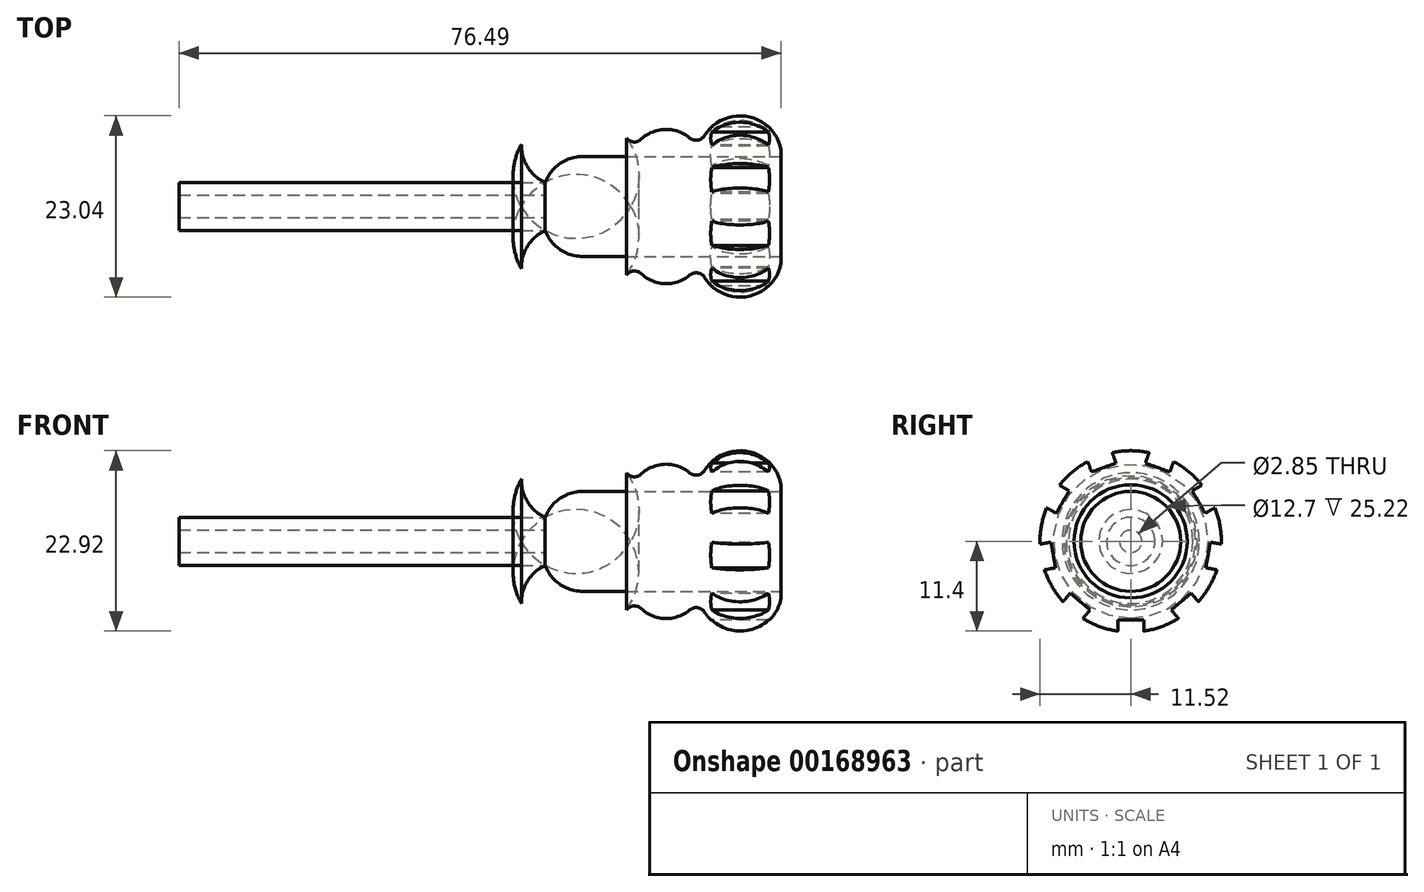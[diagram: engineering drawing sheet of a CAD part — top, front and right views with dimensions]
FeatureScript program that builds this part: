
annotation { "Feature Type Name" : "Feature", "Feature Type Description" : "" }
export const myFeature = defineFeature(function(context is Context, id is Id, definition is map)
    precondition{}
    {
        {
            var Q0;
            Q0=qCreatedBy(makeId("Front.planeOp"),FACE);
            var sketch = newSketch(context, id + "F0", { "sketchPlane" : qUnion([Q0])});
            skLineSegment(sketch, "E0.bottom", {"start": v(0, 0) * mm, "end": v(-76.5, 0) * mm});
            skLineSegment(sketch, "E0.top", {"start": v(0, 3.07) * mm, "end": v(-76.5, 3.07) * mm});
            skLineSegment(sketch, "E0.left", {"start": v(0, 0) * mm, "end": v(0, 3.07) * mm});
            skLineSegment(sketch, "E0.right", {"start": v(-76.5, 0) * mm, "end": v(-76.5, 3.07) * mm});
            skLineSegment(sketch, "E1.bottom", {"start": v(0, 0) * mm, "end": v(-33, 0) * mm});
            skLineSegment(sketch, "E1.top", {"start": v(0, 13.87) * mm, "end": v(-33, 13.87) * mm});
            skLineSegment(sketch, "E1.left", {"start": v(0, 0) * mm, "end": v(0, 13.87) * mm});
            skLineSegment(sketch, "E1.right", {"start": v(-33, 0) * mm, "end": v(-33, 13.87) * mm});
            skArc(sketch, "E2", {"start": v(-19.67, 8.7) * mm, "mid": v(-21.57, 10.52) * mm, "end": v(-23.95, 11.62) * mm});
            skArc(sketch, "E3", {"start": v(-11.61, 8.71) * mm, "mid": v(-14.73, 9.8) * mm, "end": v(-17.78, 8.54) * mm});
            skArc(sketch, "E4", {"start": v(0, 7.2) * mm, "mid": v(-0.74, 9.07) * mm, "end": v(-2.13, 10.53) * mm});
            skPoint(sketch, "E5.visualSharp", {"position": v(-18.78, 7.2) * mm});
            skArc(sketch, "E5.filletArc", {"start": v(-19.67, 8.7) * mm, "mid": v(-18.76, 8.2) * mm, "end": v(-17.78, 8.54) * mm});
            skPoint(sketch, "E6.visualSharp", {"position": v(-10.43, 7.2) * mm});
            skArc(sketch, "E6.filletArc", {"start": v(-11.61, 8.71) * mm, "mid": v(-10.6, 8.43) * mm, "end": v(-9.72, 9.01) * mm});
            skArc(sketch, "E7", {"start": v(-2.13, 10.53) * mm, "mid": v(-4.59, 11.48) * mm, "end": v(-7.2, 11.13) * mm});
            skArc(sketch, "E8", {"start": v(-7.2, 11.13) * mm, "mid": v(-8.63, 10.27) * mm, "end": v(-9.72, 9.01) * mm});
            skArc(sketch, "E9", {"start": v(-23.95, 11.62) * mm, "mid": v(-26.68, 11.88) * mm, "end": v(-29.34, 11.2) * mm});
            skArc(sketch, "E10", {"start": v(-29.34, 11.2) * mm, "mid": v(-31.43, 9.84) * mm, "end": v(-33, 7.9) * mm});
            skSolve(sketch);
        }
        {
            var Q0;
            {var subQ0=sQuery(id+"F0.wireOp",EDGE,"E2");Q0=makeQuery(id+"F0.imprint","IMPRINT",FACE,{"disambiguationData":[TD([[makeQuery(id+"F0.imprint","IMPRINT",EDGE,{"derivedFrom":subQ0}),1.0]])]});}
            var Q1;
            {var subQ5=sQuery(id+"F0.wireOp",EDGE,"E1.bottom");Q1=makeQuery(id+"F0.imprint","IMPRINT",FACE,{"disambiguationData":[TD([[makeQuery(id+"F0.imprint","IMPRINT",EDGE,{"derivedFrom":subQ5}),-1.0]])]});}
            var Q2;
            Q2=sQuery(id+"F0.wireOp",EDGE,"E0.bottom");
            revolve(context, id + "F1", {"entities" : qUnion([Q0, Q1]), "axis" : qUnion([Q2]), "revolveType" : RevolveType.FULL});
        }
        {
            var Q0;
            {var subQ0=sQuery(id+"F0.wireOp",EDGE,"E0.bottom");Q0=makeQuery(id+"F0.imprint","IMPRINT",FACE,{"disambiguationData":[TD([[makeQuery(id+"F0.imprint","IMPRINT",EDGE,{"derivedFrom":subQ0}),-1.0]])]});}
            var Q1;
            Q1=sQuery(id+"F0.wireOp",EDGE,"E0.bottom");
            revolve(context, id + "F2", {"entities" : qUnion([Q0]), "axis" : qUnion([Q1]), "revolveType" : RevolveType.FULL});
        }
        {
            var Q0;
            Q0=qCreatedBy(makeId("Right.planeOp"),FACE);
            var sketch = newSketch(context, id + "F3", { "sketchPlane" : qUnion([Q0])});
            skPoint(sketch, "E11.middle", {"position": v(0, -13.8) * mm});
            skLineSegment(sketch, "E12.bottom", {"start": v(-1.65, -17.6) * mm, "end": v(1.65, -17.6) * mm});
            skLineSegment(sketch, "E12.top", {"start": v(-1.65, -9.98) * mm, "end": v(1.65, -9.98) * mm});
            skLineSegment(sketch, "E12.left", {"start": v(-1.65, -17.6) * mm, "end": v(-1.65, -9.98) * mm});
            skLineSegment(sketch, "E12.right", {"start": v(1.65, -17.6) * mm, "end": v(1.65, -9.98) * mm});
            skLineSegment(sketch, "E13", {"start": v(-18.24, 0) * mm, "end": v(19.93, 0) * mm, "construction": true});
            skLineSegment(sketch, "E14", {"start": v(0, -29.13) * mm, "end": v(0, 16.66) * mm, "construction": true});
            skLineSegment(sketch, "E15.1.0", {"start": v(12.58, -12.42) * mm, "end": v(7.68, -6.59) * mm});
            skLineSegment(sketch, "E15.1.1", {"start": v(10.05, -14.55) * mm, "end": v(5.15, -8.7) * mm});
            skLineSegment(sketch, "E15.1.2", {"start": v(10.05, -14.55) * mm, "end": v(12.58, -12.42) * mm});
            skLineSegment(sketch, "E15.1.3", {"start": v(5.15, -8.7) * mm, "end": v(7.68, -6.59) * mm});
            skLineSegment(sketch, "E15.2.0", {"start": v(17.62, -1.43) * mm, "end": v(10.12, -0.1) * mm});
            skLineSegment(sketch, "E15.2.1", {"start": v(17.05, -4.68) * mm, "end": v(9.54, -3.36) * mm});
            skLineSegment(sketch, "E15.2.2", {"start": v(17.05, -4.68) * mm, "end": v(17.62, -1.43) * mm});
            skLineSegment(sketch, "E15.2.3", {"start": v(9.54, -3.36) * mm, "end": v(10.12, -0.1) * mm});
            skLineSegment(sketch, "E15.3.0", {"start": v(14.42, 10.23) * mm, "end": v(7.82, 6.42) * mm});
            skLineSegment(sketch, "E15.3.1", {"start": v(16.07, 7.37) * mm, "end": v(9.47, 3.56) * mm});
            skLineSegment(sketch, "E15.3.2", {"start": v(16.07, 7.37) * mm, "end": v(14.42, 10.23) * mm});
            skLineSegment(sketch, "E15.3.3", {"start": v(9.47, 3.56) * mm, "end": v(7.82, 6.42) * mm});
            skLineSegment(sketch, "E15.4.0", {"start": v(4.47, 17.1) * mm, "end": v(1.86, 9.94) * mm});
            skLineSegment(sketch, "E15.4.1", {"start": v(7.57, 15.98) * mm, "end": v(4.97, 8.82) * mm});
            skLineSegment(sketch, "E15.4.2", {"start": v(7.57, 15.98) * mm, "end": v(4.47, 17.1) * mm});
            skLineSegment(sketch, "E15.4.3", {"start": v(4.97, 8.82) * mm, "end": v(1.86, 9.94) * mm});
            skLineSegment(sketch, "E15.5.0", {"start": v(-7.57, 15.98) * mm, "end": v(-4.97, 8.82) * mm});
            skLineSegment(sketch, "E15.5.1", {"start": v(-4.47, 17.1) * mm, "end": v(-1.86, 9.94) * mm});
            skLineSegment(sketch, "E15.5.2", {"start": v(-4.47, 17.1) * mm, "end": v(-7.57, 15.98) * mm});
            skLineSegment(sketch, "E15.5.3", {"start": v(-1.86, 9.94) * mm, "end": v(-4.97, 8.82) * mm});
            skLineSegment(sketch, "E15.6.0", {"start": v(-16.07, 7.37) * mm, "end": v(-9.47, 3.56) * mm});
            skLineSegment(sketch, "E15.6.1", {"start": v(-14.42, 10.23) * mm, "end": v(-7.82, 6.42) * mm});
            skLineSegment(sketch, "E15.6.2", {"start": v(-14.42, 10.23) * mm, "end": v(-16.07, 7.37) * mm});
            skLineSegment(sketch, "E15.6.3", {"start": v(-7.82, 6.42) * mm, "end": v(-9.47, 3.56) * mm});
            skLineSegment(sketch, "E15.7.0", {"start": v(-17.05, -4.68) * mm, "end": v(-9.54, -3.36) * mm});
            skLineSegment(sketch, "E15.7.1", {"start": v(-17.62, -1.43) * mm, "end": v(-10.12, -0.1) * mm});
            skLineSegment(sketch, "E15.7.2", {"start": v(-17.62, -1.43) * mm, "end": v(-17.05, -4.68) * mm});
            skLineSegment(sketch, "E15.7.3", {"start": v(-10.12, -0.1) * mm, "end": v(-9.54, -3.36) * mm});
            skLineSegment(sketch, "E15.8.0", {"start": v(-10.05, -14.55) * mm, "end": v(-5.15, -8.7) * mm});
            skLineSegment(sketch, "E15.8.1", {"start": v(-12.58, -12.42) * mm, "end": v(-7.68, -6.59) * mm});
            skLineSegment(sketch, "E15.8.2", {"start": v(-12.58, -12.42) * mm, "end": v(-10.05, -14.55) * mm});
            skLineSegment(sketch, "E15.8.3", {"start": v(-7.68, -6.59) * mm, "end": v(-5.15, -8.7) * mm});
            skPoint(sketch, "E15.center", {"position": v(0, 0) * mm});
            skSolve(sketch);
        }
        {
            var Q0;
            Q0=qCreatedBy(makeId("Right.planeOp"),FACE);
            var sketch = newSketch(context, id + "F4", { "sketchPlane" : qUnion([Q0])});
            skCircle(sketch, "E16", {"center": v(0, 0) * mm, "radius": 6.35 * mm});
            skCircle(sketch, "E17", {"center": v(0, 0) * mm, "radius": 1.42 * mm});
            skSolve(sketch);
        }
        {
            var Q0;
            Q0=makeQuery(id+"F3.imprint","IMPRINT",FACE,{"disambiguationData":[TD([[makeQuery(id+"F3.imprint","IMPRINT",EDGE,{"derivedFrom":sQuery(id+"F3.wireOp",EDGE,"E15.6.0")}),1.0]])]});
            var Q1;
            Q1=makeQuery(id+"F3.imprint","IMPRINT",FACE,{"disambiguationData":[TD([[makeQuery(id+"F3.imprint","IMPRINT",EDGE,{"derivedFrom":sQuery(id+"F3.wireOp",EDGE,"E15.7.0")}),1.0]])]});
            var Q2;
            Q2=makeQuery(id+"F3.imprint","IMPRINT",FACE,{"disambiguationData":[TD([[makeQuery(id+"F3.imprint","IMPRINT",EDGE,{"derivedFrom":sQuery(id+"F3.wireOp",EDGE,"E15.8.0")}),1.0]])]});
            var Q3;
            Q3=makeQuery(id+"F3.imprint","IMPRINT",FACE,{"disambiguationData":[TD([[makeQuery(id+"F3.imprint","IMPRINT",EDGE,{"derivedFrom":sQuery(id+"F3.wireOp",EDGE,"E15.5.0")}),1.0]])]});
            var Q4;
            Q4=makeQuery(id+"F3.imprint","IMPRINT",FACE,{"disambiguationData":[TD([[makeQuery(id+"F3.imprint","IMPRINT",EDGE,{"derivedFrom":sQuery(id+"F3.wireOp",EDGE,"E15.4.0")}),1.0]])]});
            var Q5;
            Q5=makeQuery(id+"F3.imprint","IMPRINT",FACE,{"disambiguationData":[TD([[makeQuery(id+"F3.imprint","IMPRINT",EDGE,{"derivedFrom":sQuery(id+"F3.wireOp",EDGE,"E12.bottom")}),1.0]])]});
            var Q6;
            Q6=makeQuery(id+"F3.imprint","IMPRINT",FACE,{"disambiguationData":[TD([[makeQuery(id+"F3.imprint","IMPRINT",EDGE,{"derivedFrom":sQuery(id+"F3.wireOp",EDGE,"E15.1.0")}),1.0]])]});
            var Q7;
            Q7=makeQuery(id+"F3.imprint","IMPRINT",FACE,{"disambiguationData":[TD([[makeQuery(id+"F3.imprint","IMPRINT",EDGE,{"derivedFrom":sQuery(id+"F3.wireOp",EDGE,"E15.2.0")}),1.0]])]});
            var Q8;
            Q8=makeQuery(id+"F3.imprint","IMPRINT",FACE,{"disambiguationData":[TD([[makeQuery(id+"F3.imprint","IMPRINT",EDGE,{"derivedFrom":sQuery(id+"F3.wireOp",EDGE,"E15.3.0")}),1.0]])]});
            extrude(context, id + "F5", {"entities" : qUnion([Q0, Q1, Q2, Q3, Q4, Q5, Q6, Q7, Q8]), "operationType" : NewBodyOperationType.REMOVE, "depth" : 2.3 * mm, "hasSecondDirection" : true, "secondDirectionOppositeDirection" : true, "secondDirectionDepth" : 12.2 * mm});
        }
        {
            var Q0;
            Q0=makeQuery(id+"F4.imprint","IMPRINT",FACE,{"disambiguationData":[TD([[makeQuery(id+"F4.imprint","IMPRINT",EDGE,{"derivedFrom":sQuery(id+"F4.wireOp",EDGE,"E16")}),1.0]])]});
            extrude(context, id + "F6", {"entities" : qUnion([Q0]), "operationType" : NewBodyOperationType.REMOVE, "oppositeDirection" : true, "depth" : 29.97 * mm});
        }
        {
            var Q0;
            Q0=makeQuery(id+"F4.imprint","IMPRINT",FACE,{"disambiguationData":[TD([[makeQuery(id+"F4.imprint","IMPRINT",EDGE,{"derivedFrom":sQuery(id+"F4.wireOp",EDGE,"E17")}),1.0]])]});
            extrude(context, id + "F7", {"entities" : qUnion([Q0]), "operationType" : NewBodyOperationType.REMOVE, "oppositeDirection" : true, "depth" : 90.83 * mm});
        }
        {
            var Q0;
            Q0=sQuery(id+"F0.wireOp",EDGE,"E7");
            var Q1;
            Q1=sQuery(id+"F0.wireOp",EDGE,"E9");
            var Q2;
            Q2=sQuery(id+"F0.wireOp",EDGE,"E3");
            var Q3;
            Q3=sQuery(id+"F0.wireOp",EDGE,"E0.bottom");
            revolve(context, id + "F8", {"bodyType" : ToolBodyType.SURFACE, "surfaceEntities" : qUnion([Q0, Q1, Q2]), "axis" : qUnion([Q3]), "revolveType" : RevolveType.FULL});
        }
        {
            var Q0;
            Q0=makeQuery(id+"F1.opRevolve","SWEPT_EDGE",EDGE,{"disambiguationData":[OSD([sQuery(id+"F0.wireOp",EDGE,"E0.top"),sQuery(id+"F0.wireOp",EDGE,"E1.right")])]});
            var Q1;
            Q1=makeQuery(id+"F6.boolean.opBoolean","COPY",EDGE,{"derivedFrom":makeQuery(id+"F6.opExtrude","CAP_EDGE",EDGE,{"disambiguationData":[OSD([sQuery(id+"F4.wireOp",EDGE,"E16")])],"isStart":false})});
            var Q2;
            Q2=makeQuery(id+"F6.boolean.opBoolean","COPY",EDGE,{"derivedFrom":makeQuery(id+"F6.opExtrude","CAP_EDGE",EDGE,{"disambiguationData":[OSD([sQuery(id+"F4.wireOp",EDGE,"E16")])],"isStart":true})});
            fillet(context, id + "F9", {"entities" : qUnion([Q0, Q1, Q2]), "radius" : 5.08 * mm, "tangentPropagation" : true, "allowEdgeOverflow" : false});
        }
    });
